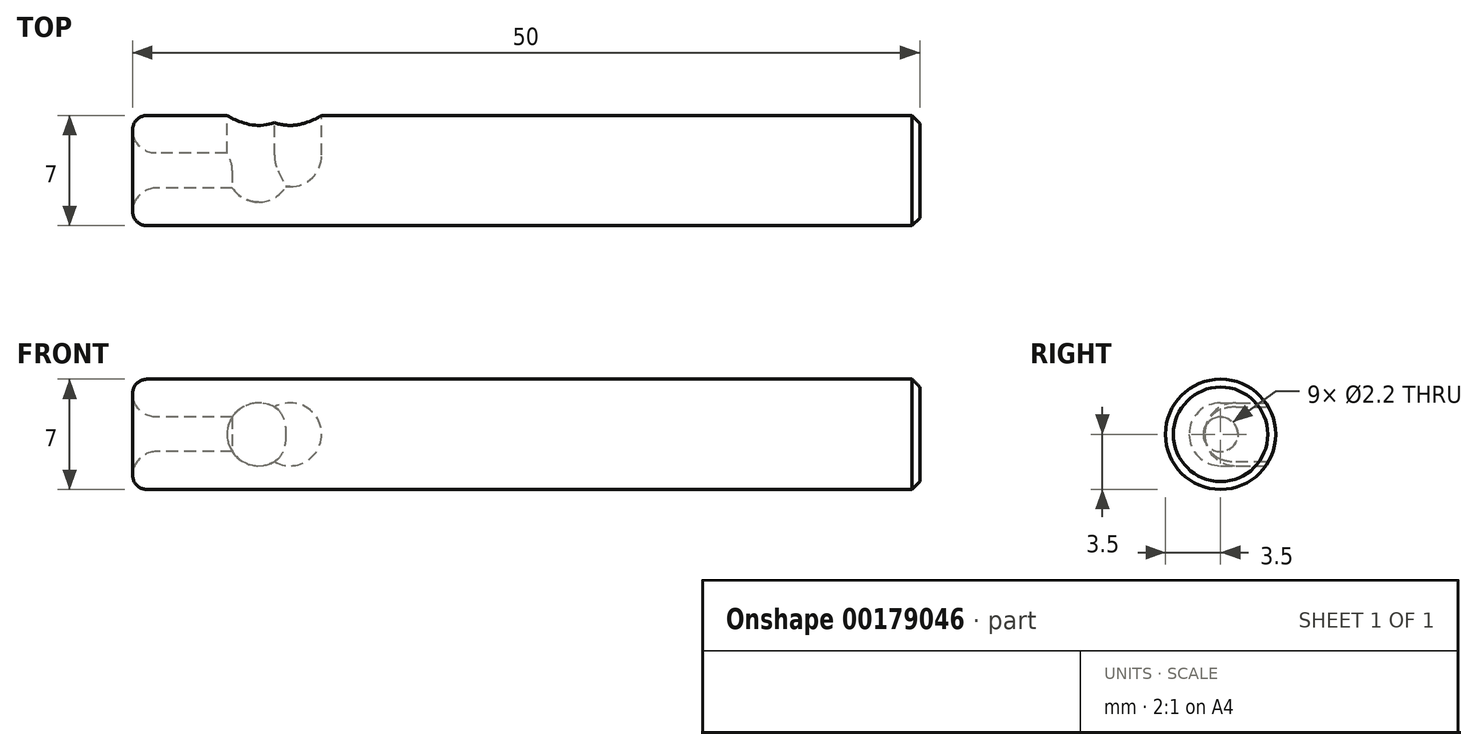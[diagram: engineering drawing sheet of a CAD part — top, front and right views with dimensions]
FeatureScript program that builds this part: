
annotation { "Feature Type Name" : "Feature", "Feature Type Description" : "" }
export const myFeature = defineFeature(function(context is Context, id is Id, definition is map)
    precondition{}
    {
        {
            var Q0;
            Q0=qCreatedBy(makeId("Front.planeOp"),FACE);
            var sketch = newSketch(context, id + "F0", { "sketchPlane" : qUnion([Q0])});
            skLineSegment(sketch, "E0", {"start": v(-49.1, 3.5) * mm, "end": v(0, 3.5) * mm});
            skLineSegment(sketch, "E1", {"start": v(-48.5, 1.1) * mm, "end": v(-48.5, 0) * mm});
            skArc(sketch, "E2", {"start": v(-48.5, 1.1) * mm, "mid": v(-49.56, 1.54) * mm, "end": v(-50, 2.6) * mm});
            skArc(sketch, "E3", {"start": v(-50, 2.6) * mm, "mid": v(-49.74, 3.24) * mm, "end": v(-49.1, 3.5) * mm});
            skLineSegment(sketch, "E4", {"start": v(0, 3.5) * mm, "end": v(0, 0) * mm});
            skLineSegment(sketch, "E5", {"start": v(0, 0) * mm, "end": v(-48.5, 0) * mm});
            skSolve(sketch);
        }
        {
            var Q0;
            Q0 = qSketchRegion(id + "F0", true);
            var Q1;
            Q1=sQuery(id+"F0.wireOp",EDGE,"E5");
            revolve(context, id + "F1", {"entities" : qUnion([Q0]), "axis" : qUnion([Q1]), "revolveType" : RevolveType.FULL});
        }
        {
            var Q0;
            Q0=makeQuery(id+"F1.opRevolve","SWEPT_FACE",FACE,{"disambiguationData":[OSD([sQuery(id+"F0.wireOp",EDGE,"E1")])]});
            extrude(context, id + "F2", {"entities" : qUnion([Q0]), "operationType" : NewBodyOperationType.REMOVE, "oppositeDirection" : true, "depth" : 5 * mm});
        }
        {
            var Q0;
            Q0=makeQuery(id+"F1.opRevolve","SWEPT_EDGE",EDGE,{"disambiguationData":[OSD([sQuery(id+"F0.wireOp",EDGE,"E0"),sQuery(id+"F0.wireOp",EDGE,"E4")])]});
            chamfer(context, id + "F3", {"entities" : qUnion([Q0]), "width" : 0.5 * mm, "tangentPropagation" : true});
        }
        {
            var Q0;
            Q0=qCreatedBy(makeId("Top.planeOp"),FACE);
            var sketch = newSketch(context, id + "F4", { "sketchPlane" : qUnion([Q0])});
            skLineSegment(sketch, "E6", {"start": v(-44, 7.95) * mm, "end": v(-44, 0) * mm});
            skArc(sketch, "E7", {"start": v(-44, 0) * mm, "mid": v(-43.41, -1.41) * mm, "end": v(-42, -2) * mm});
            skLineSegment(sketch, "E8", {"start": v(-42, -2) * mm, "end": v(-42, 7.95) * mm});
            skLineSegment(sketch, "E9", {"start": v(-42, 7.95) * mm, "end": v(-44, 7.95) * mm});
            skLineSegment(sketch, "E10", {"start": v(-42, -2) * mm, "end": v(-37.02, -2) * mm, "construction": true});
            skSolve(sketch);
        }
        {
            var Q0;
            Q0 = qSketchRegion(id + "F4", true);
            var Q1;
            Q1=sQuery(id+"F4.wireOp",EDGE,"E8");
            revolve(context, id + "F5", {"operationType" : NewBodyOperationType.REMOVE, "entities" : qUnion([Q0]), "axis" : qUnion([Q1]), "revolveType" : RevolveType.FULL, "oppositeDirection" : true});
        }
        {
            var Q0;
            Q0=qCreatedBy(makeId("Top.planeOp"),FACE);
            var sketch = newSketch(context, id + "F6", { "sketchPlane" : qUnion([Q0])});
            skLineSegment(sketch, "E11", {"start": v(-42, 6.12) * mm, "end": v(-42, 0.97) * mm});
            skArc(sketch, "E12", {"start": v(-42, 0.97) * mm, "mid": v(-41.41, -0.44) * mm, "end": v(-40, -1.03) * mm});
            skLineSegment(sketch, "E13", {"start": v(-40, -1.03) * mm, "end": v(-40, 6.12) * mm});
            skLineSegment(sketch, "E14", {"start": v(-42, 6.12) * mm, "end": v(-40, 6.12) * mm});
            skLineSegment(sketch, "E15", {"start": v(-40, 3.5) * mm, "end": v(-40, 0) * mm});
            skLineSegment(sketch, "E16", {"start": v(-44, 1.1) * mm, "end": v(-44, 3.5) * mm});
            skSolve(sketch);
        }
        {
            var Q0;
            Q0=makeQuery(id+"F6.imprint","IMPRINT",FACE,{"disambiguationData":[TD([[makeQuery(id+"F6.imprint","IMPRINT",EDGE,{"derivedFrom":sQuery(id+"F6.wireOp",EDGE,"E11")}),1.0]])]});
            var Q1;
            Q1=sQuery(id+"F6.wireOp",EDGE,"E13");
            revolve(context, id + "F7", {"operationType" : NewBodyOperationType.REMOVE, "entities" : qUnion([Q0]), "axis" : qUnion([Q1]), "revolveType" : RevolveType.FULL, "oppositeDirection" : true});
        }
    });
